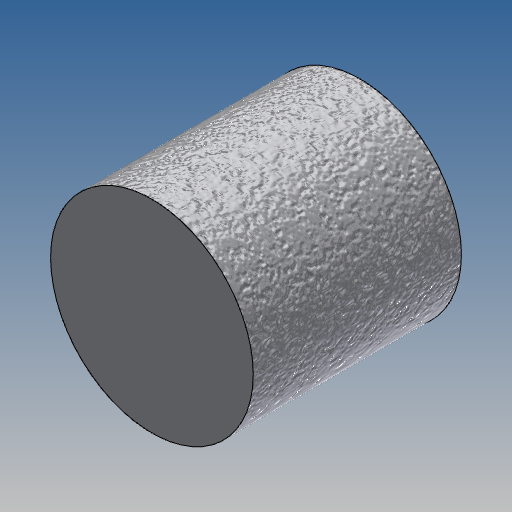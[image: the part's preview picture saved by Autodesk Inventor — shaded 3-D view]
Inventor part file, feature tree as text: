
AUTODESK INVENTOR PART (.ipt)
format: ipt  version: 2018.3 (Build 223284000, 284)  size: 224,256 bytes
history: native  units: in
note: dims shown in document units (in); Inventor stores cm internally (conversion verified against a paired STEP export)
features: extrude x1, sketch x1
ambient origin geometry x8: Origin, YZ Plane, XZ Plane, XY Plane, X Axis, Y Axis, Z Axis, Center Point
bodies: Solid1 (feature_tree)
feature tree (2):
  extrude  "Extrusion1"  Depth=1.1024in TaperAngle=0.0deg
  sketch  "Sketch1"  dims[d0=1.0728in d1=1.1024in d2=0.0in]
